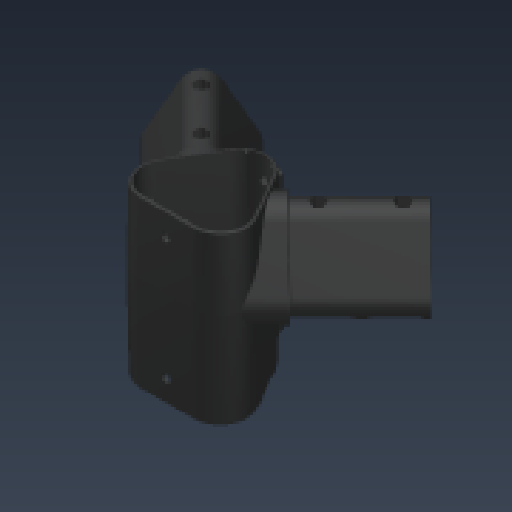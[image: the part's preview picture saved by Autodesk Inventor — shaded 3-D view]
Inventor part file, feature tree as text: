
AUTODESK INVENTOR PART (.ipt)
format: ipt  version: 2024.3 (Build 283343000, 343)  size: 2,960,896 bytes
history: native  units: in
note: dims shown in document units (in); Inventor stores cm internally (conversion verified against a paired STEP export)
features: fillet x1
ambient origin geometry x8: Origin, YZ Plane, XZ Plane, XY Plane, X Axis, Y Axis, Z Axis, Center Point
bodies: Solid1 (feature_tree)
feature tree (1):
  fillet  "Fillet138"  [1 undecoded]
note: 1 required parameter value undecoded (feature->parameter linkage not recoverable at this tier; creation-order binding heuristic only, values carry confidence <= 0.55)
